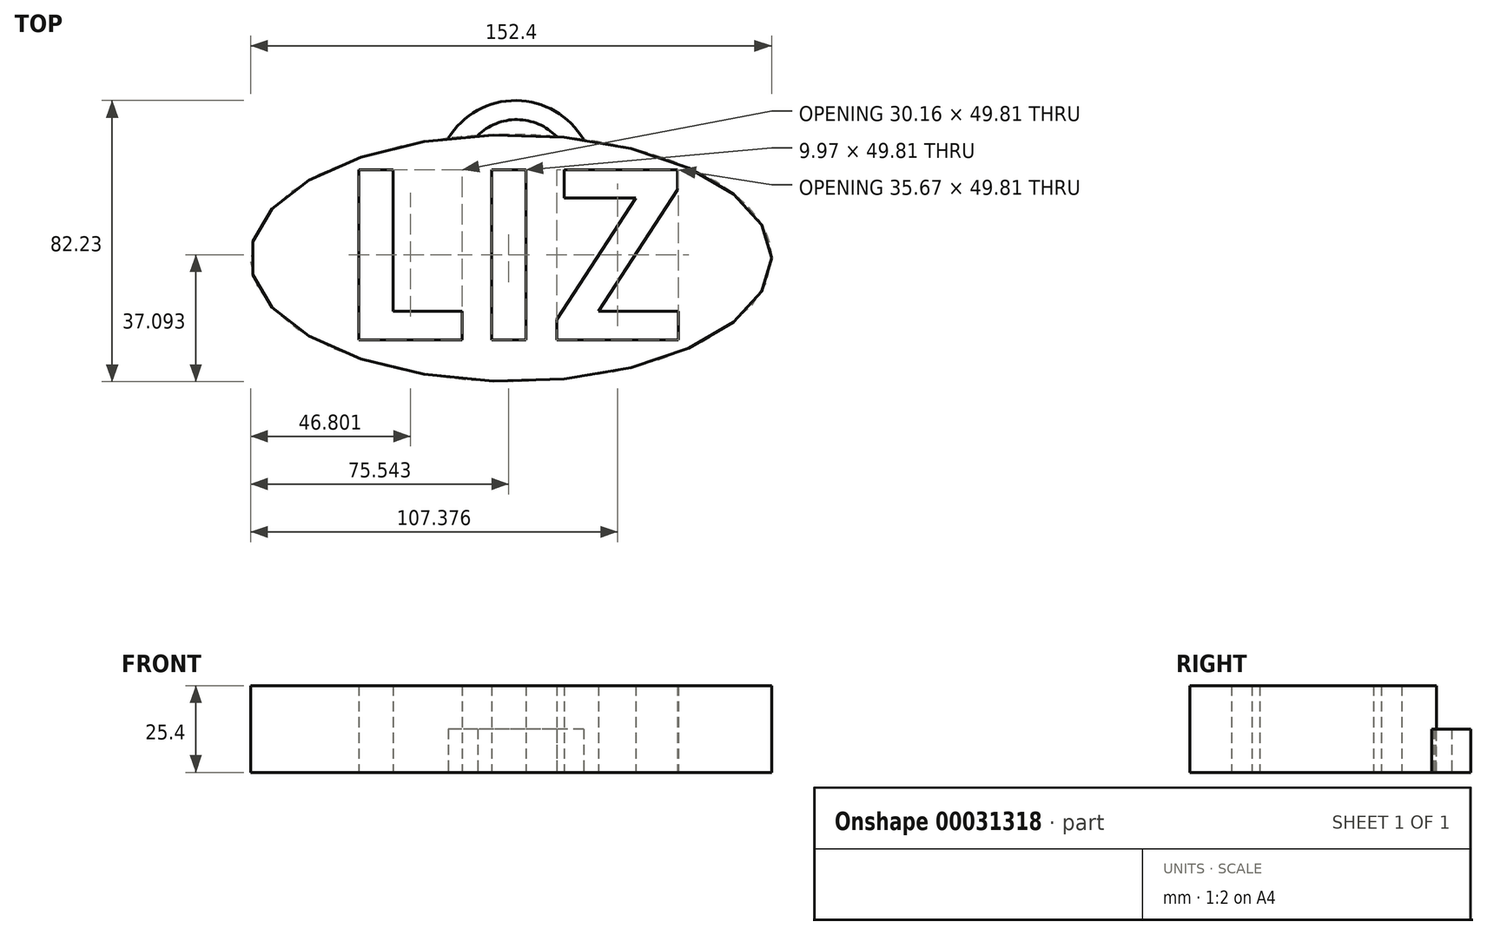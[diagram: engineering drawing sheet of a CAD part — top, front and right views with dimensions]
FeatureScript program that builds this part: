
annotation { "Feature Type Name" : "Feature", "Feature Type Description" : "" }
export const myFeature = defineFeature(function(context is Context, id is Id, definition is map)
    precondition{}
    {
        {
            var Q0;
            Q0=qCreatedBy(makeId("Top.planeOp"),FACE);
            var sketch = newSketch(context, id + "F0", { "sketchPlane" : qUnion([Q0])});
            skEllipse(sketch, "E0", {"center": v(0, 0) * mm, "majorRadius": 76.2 * mm, "minorRadius": 36.12 * mm, "majorAxis": v(1, 0)});
            skText(sketch, "E1", { "text": "LIZ", "fontName": "NotoSansCJKsc-Bold.otf"});
            skArc(sketch, "E2", {"start": v(21.23, 34.69) * mm, "mid": v(1.55, 46.11) * mm, "end": v(-18.35, 35.06) * mm});
            skArc(sketch, "E3", {"start": v(13.34, 35.56) * mm, "mid": v(1.85, 40.53) * mm, "end": v(-9.76, 35.82) * mm});
            const initialGuessF0  = {"E1": [-0.0506, -0.02393, 1, 0, 0.04846]};
            skSetInitialGuess(sketch, initialGuessF0);
            skSolve(sketch);
        }
        {
            var Q0;
            Q0=makeQuery(id+"F0.imprint","IMPRINT",FACE,{"disambiguationData":[TD([[makeQuery(id+"F0.imprint","IMPRINT",EDGE,{"derivedFrom":sQuery(id+"F0.wireOp",EDGE,"E0")}),1.0]])]});
            extrude(context, id + "F1", {"entities" : qUnion([Q0]), "depth" : 25.4 * mm});
        }
        {
            var Q0;
            Q0 = qSketchRegion(id + "F0", true);
            extrude(context, id + "F2", {"entities" : qUnion([Q0]), "operationType" : NewBodyOperationType.ADD, "depth" : 12.7 * mm});
        }
    });
